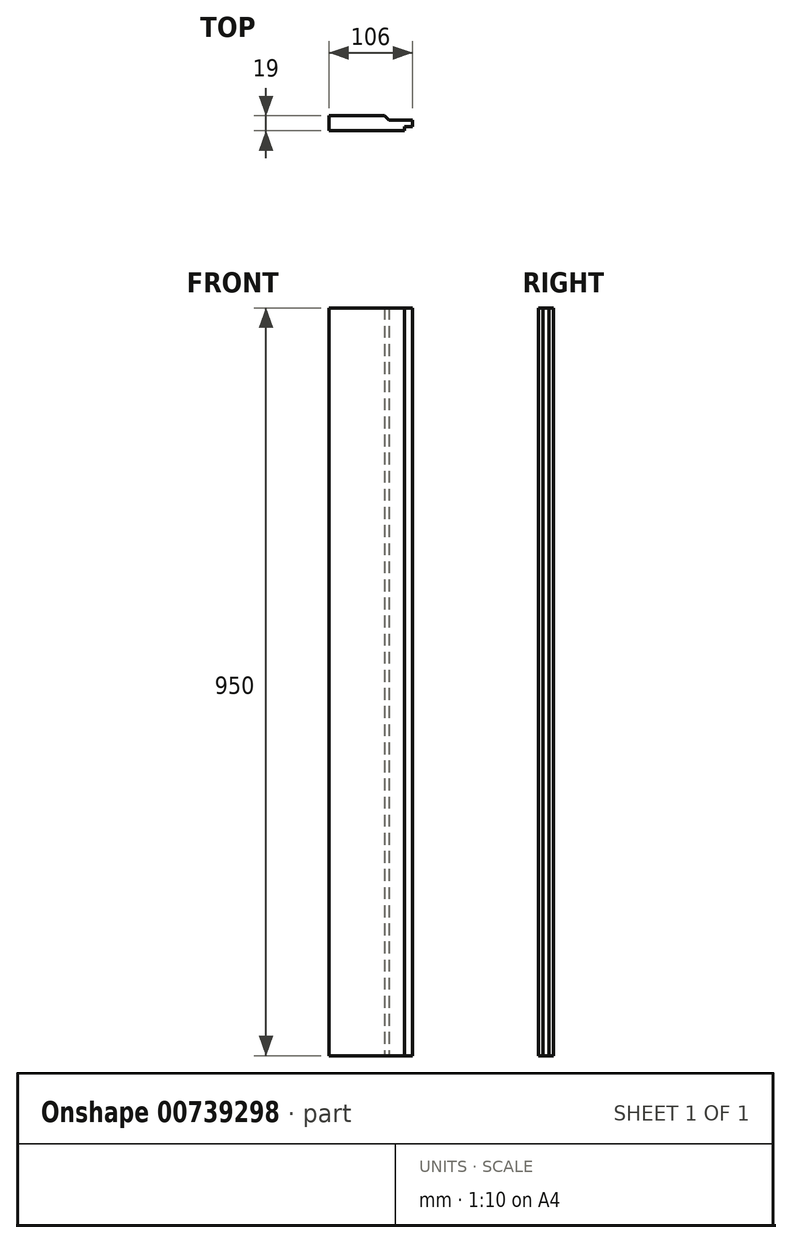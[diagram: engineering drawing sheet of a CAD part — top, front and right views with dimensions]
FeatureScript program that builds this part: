
annotation { "Feature Type Name" : "Feature", "Feature Type Description" : "" }
export const myFeature = defineFeature(function(context is Context, id is Id, definition is map)
    precondition{}
    {
        {
            var Q0;
            Q0=qCreatedBy(makeId("Top.planeOp"),FACE);
            var sketch = newSketch(context, id + "F0", { "sketchPlane" : qUnion([Q0])});
            skLineSegment(sketch, "E0.bottom", {"start": v(0, -9.5) * mm, "end": v(136, -9.5) * mm});
            skLineSegment(sketch, "E0.top", {"start": v(0, 9.5) * mm, "end": v(110.5, 9.5) * mm});
            skLineSegment(sketch, "E0.left", {"start": v(0, -9.5) * mm, "end": v(0, -4) * mm});
            skLineSegment(sketch, "E0.right", {"start": v(136, -9.5) * mm, "end": v(136, -4) * mm});
            skLineSegment(sketch, "E1", {"start": v(0, -4) * mm, "end": v(12, -4) * mm});
            skLineSegment(sketch, "E2", {"start": v(12, -4) * mm, "end": v(12, 4) * mm});
            skLineSegment(sketch, "E3", {"start": v(12, 4) * mm, "end": v(0, 4) * mm});
            skLineSegment(sketch, "E4.trimOffspring", {"start": v(0, 4) * mm, "end": v(0, 9.5) * mm});
            skLineSegment(sketch, "E5", {"start": v(136, -4) * mm, "end": v(146, -4) * mm});
            skLineSegment(sketch, "E6", {"start": v(146, -4) * mm, "end": v(146, 4) * mm});
            skLineSegment(sketch, "E7", {"start": v(146, 4) * mm, "end": v(116, 4) * mm});
            skLineSegment(sketch, "E8.trimOffspring", {"start": v(116, 4) * mm, "end": v(110.5, 9.5) * mm});
            skSolve(sketch);
        }
        {
            var Q0;
            Q0=makeQuery(id+"F0.imprint","IMPRINT",FACE,{"disambiguationData":[TD([[makeQuery(id+"F0.imprint","IMPRINT",EDGE,{"derivedFrom":sQuery(id+"F0.wireOp",EDGE,"E0.bottom")}),1.0]])]});
            extrude(context, id + "F1", {"entities" : qUnion([Q0]), "depth" : 950 * mm, "offsetDistance" : 25 * mm});
        }
        {
            var Q0;
            Q0=makeQuery(id+"F1.opExtrude","CAP_FACE",FACE,{"disambiguationData":[OSD([sQuery(id+"F0.wireOp",EDGE,"E0.bottom"),sQuery(id+"F0.wireOp",EDGE,"E0.top"),sQuery(id+"F0.wireOp",EDGE,"E0.left"),sQuery(id+"F0.wireOp",EDGE,"E0.right"),sQuery(id+"F0.wireOp",EDGE,"E1"),sQuery(id+"F0.wireOp",EDGE,"E2"),sQuery(id+"F0.wireOp",EDGE,"E3"),sQuery(id+"F0.wireOp",EDGE,"E4.trimOffspring"),sQuery(id+"F0.wireOp",EDGE,"E5"),sQuery(id+"F0.wireOp",EDGE,"E6"),sQuery(id+"F0.wireOp",EDGE,"E7"),sQuery(id+"F0.wireOp",EDGE,"E8.trimOffspring")])],"isStart":true});
            var sketch = newSketch(context, id + "F2", { "sketchPlane" : qUnion([Q0])});
            skLineSegment(sketch, "E9", {"start": v(40, -9.5) * mm, "end": v(40, 9.5) * mm});
            skLineSegment(sketch, "E10", {"start": v(0, -4) * mm, "end": v(0, 4) * mm});
            skSolve(sketch);
        }
        {
            var Q0;
            {var subQ1=sQuery(id+"F2.wireOp",EDGE,"E9");Q0=makeQuery(id+"F2.imprint","IMPRINT",FACE,{"disambiguationData":[TD([[makeQuery(id+"F2.imprint","IMPRINT",EDGE,{"derivedFrom":subQ1}),1.0]])]});}
            var Q1;
            Q1=makeQuery(id+"F2.imprint","IMPRINT",FACE,{"disambiguationData":[TD([[makeQuery(id+"F2.imprint","IMPRINT",EDGE,{"derivedFrom":sQuery(id+"F2.wireOp",EDGE,"E10")}),-1.0]])]});
            extrude(context, id + "F3", {"entities" : qUnion([Q0, Q1]), "operationType" : NewBodyOperationType.REMOVE, "endBound" : BoundingType.THROUGH_ALL, "oppositeDirection" : true, "depth" : 25 * mm, "offsetDistance" : 25 * mm});
        }
    });
